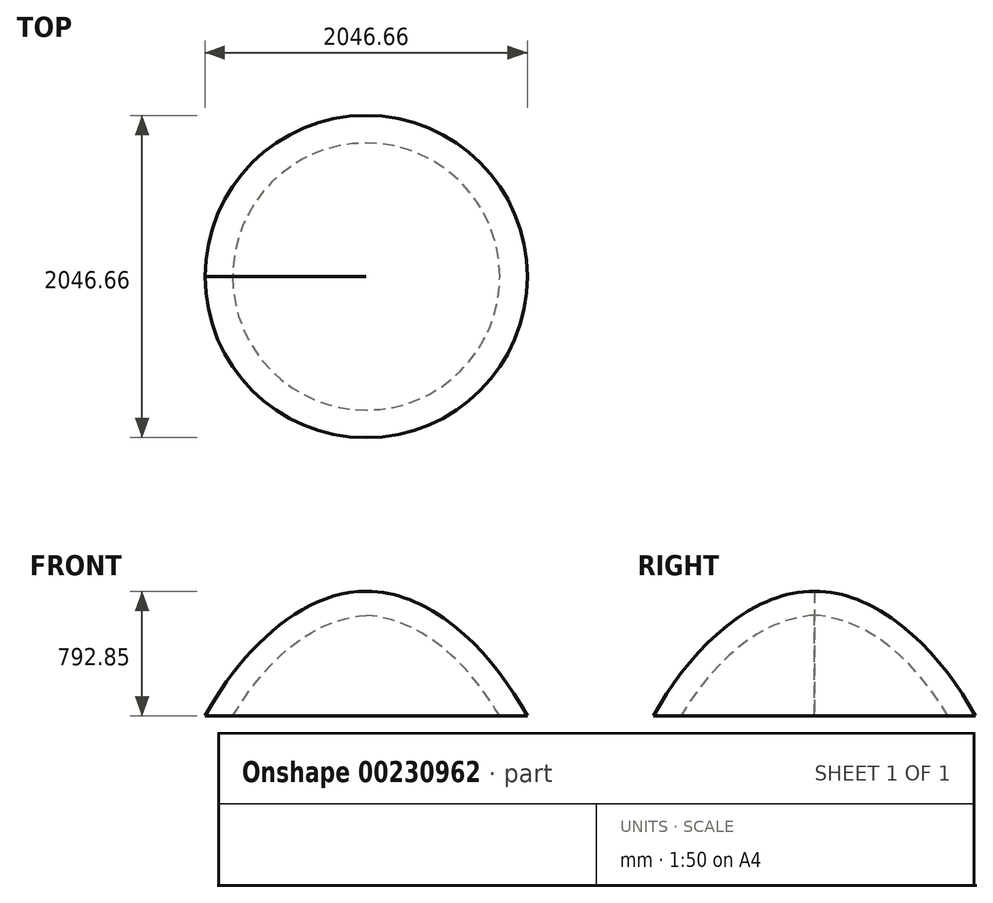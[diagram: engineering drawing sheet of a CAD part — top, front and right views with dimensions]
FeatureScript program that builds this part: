
annotation { "Feature Type Name" : "Feature", "Feature Type Description" : "" }
export const myFeature = defineFeature(function(context is Context, id is Id, definition is map)
    precondition{}
    {
        {
            var Q0;
            Q0=qCreatedBy(makeId("Front.planeOp"),FACE);
            var sketch = newSketch(context, id + "F0", { "sketchPlane" : qUnion([Q0])});
            skLineSegment(sketch, "E0", {"start": v(-1181.84, -1150.9) * mm, "end": v(-927.84, -1150.9) * mm});
            skFitSpline(sketch, "E1", {"points": [v(0, 1953.34) * mm, v(-1100.72, 1005.82) * mm, v(-1321.31, -446.03) * mm, v(-1216.83, -971.67) * mm, v(-1181.84, -1150.9) * mm], "startDerivative": vector(-4000.43, 5.06) * mm, "endDerivative": vector(0, -1489.55) * mm});
            skLineSegment(sketch, "E2", {"start": v(-1099.69, 1008.1) * mm, "end": v(-930.94, 1008.1) * mm});
            skLineSegment(sketch, "E3", {"start": v(-1181.84, -1150.9) * mm, "end": v(-1181.84, -1354.1) * mm});
            skLineSegment(sketch, "E4", {"start": v(-1181.84, -1354.1) * mm, "end": v(-877.04, -1354.1) * mm});
            skLineSegment(sketch, "E5", {"start": v(-877.04, -1354.1) * mm, "end": v(-877.04, -1252.5) * mm});
            skLineSegment(sketch, "E6", {"start": v(-877.04, -1252.5) * mm, "end": v(-927.84, -1252.5) * mm});
            skLineSegment(sketch, "E7", {"start": v(-927.84, -1252.5) * mm, "end": v(-927.84, -1150.9) * mm});
            skFitSpline(sketch, "E8.trimOffspring", {"points": [v(0, -1757.92) * mm, v(-927.84, -1150.9) * mm, v(-1179.31, -127.8) * mm, v(-917.89, 1034.08) * mm, v(0, 1800.66) * mm], "startDerivative": vector(-4973.2, 113.59) * mm, "endDerivative": vector(4756.7, 336.76) * mm});
            skLineSegment(sketch, "E9", {"start": v(-1023.33, 1160.5) * mm, "end": v(-848.12, 1160.5) * mm});
            skLineSegment(sketch, "E10", {"start": v(0, 1953.34) * mm, "end": v(0, 1800.66) * mm});
            skSolve(sketch);
        }
        {
            var Q0;
            {var subQ2=sQuery(id+"F0.wireOp",EDGE,"E9");Q0=makeQuery(id+"F0.imprint","IMPRINT",FACE,{"disambiguationData":[TD([[makeQuery(id+"F0.imprint","IMPRINT",EDGE,{"derivedFrom":subQ2}),1.0]])]});}
            var Q1;
            Q1=sQuery(id+"F0.wireOp",EDGE,"E10");
            revolve(context, id + "F1", {"entities" : qUnion([Q0]), "axis" : qUnion([Q1]), "revolveType" : RevolveType.FULL});
        }
    });
